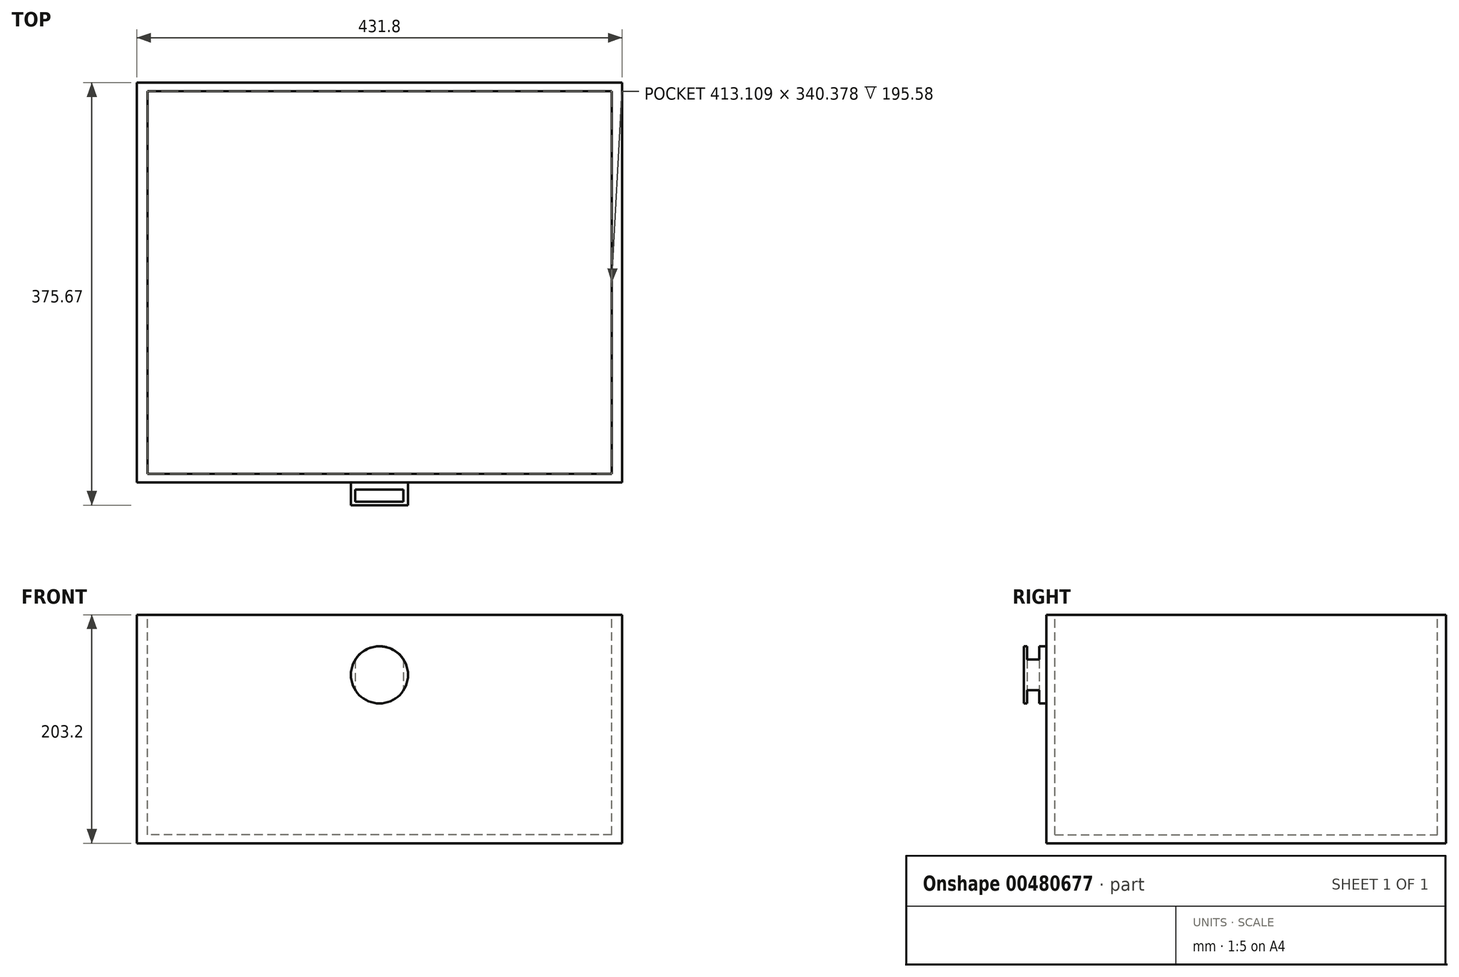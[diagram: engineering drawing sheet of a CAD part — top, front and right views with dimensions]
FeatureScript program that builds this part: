
annotation { "Feature Type Name" : "Feature", "Feature Type Description" : "" }
export const myFeature = defineFeature(function(context is Context, id is Id, definition is map)
    precondition{}
    {
        {
            var Q0;
            Q0=qCreatedBy(makeId("Front.planeOp"),FACE);
            var sketch = newSketch(context, id + "F0", { "sketchPlane" : qUnion([Q0])});
            skLineSegment(sketch, "E0.bottom", {"start": v(-215.9, 101.6) * mm, "end": v(215.9, 101.6) * mm});
            skLineSegment(sketch, "E0.top", {"start": v(-215.9, -101.6) * mm, "end": v(215.9, -101.6) * mm});
            skLineSegment(sketch, "E0.left", {"start": v(-215.9, 101.6) * mm, "end": v(-215.9, -101.6) * mm});
            skLineSegment(sketch, "E0.right", {"start": v(215.9, 101.6) * mm, "end": v(215.9, -101.6) * mm});
            skPoint(sketch, "E0.middle", {"position": v(0, 0) * mm});
            skSolve(sketch);
        }
        {
            var Q0;
            Q0 = qSketchRegion(id + "F0", true);
            extrude(context, id + "F1", {"entities" : qUnion([Q0]), "depth" : 355.6 * mm});
        }
        {
            var Q0;
            Q0=makeQuery(id+"F1.opExtrude","SWEPT_FACE",FACE,{"disambiguationData":[OSD([sQuery(id+"F0.wireOp",EDGE,"E0.bottom")])]});
            var sketch = newSketch(context, id + "F2", { "sketchPlane" : qUnion([Q0])});
            skLineSegment(sketch, "E1.bottom", {"start": v(206.67, -347.89) * mm, "end": v(-206.44, -347.89) * mm});
            skLineSegment(sketch, "E1.top", {"start": v(206.67, -7.5) * mm, "end": v(-206.44, -7.5) * mm});
            skLineSegment(sketch, "E1.left", {"start": v(206.67, -347.89) * mm, "end": v(206.67, -7.5) * mm});
            skLineSegment(sketch, "E1.right", {"start": v(-206.44, -347.89) * mm, "end": v(-206.44, -7.5) * mm});
            skSolve(sketch);
        }
        {
            var Q0;
            Q0 = qSketchRegion(id + "F2", true);
            extrude(context, id + "F3", {"entities" : qUnion([Q0]), "operationType" : NewBodyOperationType.REMOVE, "oppositeDirection" : true, "depth" : 195.58 * mm});
        }
        {
            var Q0;
            Q0=makeQuery(id+"F1.opExtrude","CAP_FACE",FACE,{"disambiguationData":[OSD([sQuery(id+"F0.wireOp",EDGE,"E0.bottom"),sQuery(id+"F0.wireOp",EDGE,"E0.top"),sQuery(id+"F0.wireOp",EDGE,"E0.left"),sQuery(id+"F0.wireOp",EDGE,"E0.right")])],"isStart":false});
            var sketch = newSketch(context, id + "F4", { "sketchPlane" : qUnion([Q0])});
            skCircle(sketch, "E2", {"center": v(0, 48.11) * mm, "radius": 25.4 * mm});
            skSolve(sketch);
        }
        {
            var Q0;
            Q0 = qSketchRegion(id + "F4", true);
            extrude(context, id + "F5", {"entities" : qUnion([Q0]), "operationType" : NewBodyOperationType.ADD, "depth" : 20.07 * mm});
        }
        {
            var Q0;
            Q0=makeQuery(id+"F3.boolean.opBoolean","COPY",FACE,{"derivedFrom":makeQuery(id+"F3.opExtrude","CAP_FACE",FACE,{"disambiguationData":[OSD([sQuery(id+"F2.wireOp",EDGE,"E1.bottom"),sQuery(id+"F2.wireOp",EDGE,"E1.top"),sQuery(id+"F2.wireOp",EDGE,"E1.left"),sQuery(id+"F2.wireOp",EDGE,"E1.right")])],"isStart":false})});
            var sketch = newSketch(context, id + "F6", { "sketchPlane" : qUnion([Q0])});
            skLineSegment(sketch, "E3.bottom", {"start": v(-21.69, -361.92) * mm, "end": v(21.37, -361.92) * mm});
            skLineSegment(sketch, "E3.top", {"start": v(-21.69, -372.68) * mm, "end": v(21.37, -372.68) * mm});
            skLineSegment(sketch, "E3.left", {"start": v(-21.69, -361.92) * mm, "end": v(-21.69, -372.68) * mm});
            skLineSegment(sketch, "E3.right", {"start": v(21.37, -361.92) * mm, "end": v(21.37, -372.68) * mm});
            skSolve(sketch);
        }
        {
            var Q0;
            Q0 = qSketchRegion(id + "F6", true);
            extrude(context, id + "F7", {"entities" : qUnion([Q0]), "operationType" : NewBodyOperationType.REMOVE, "endBound" : BoundingType.THROUGH_ALL, "depth" : 25.4 * mm});
        }
    });
